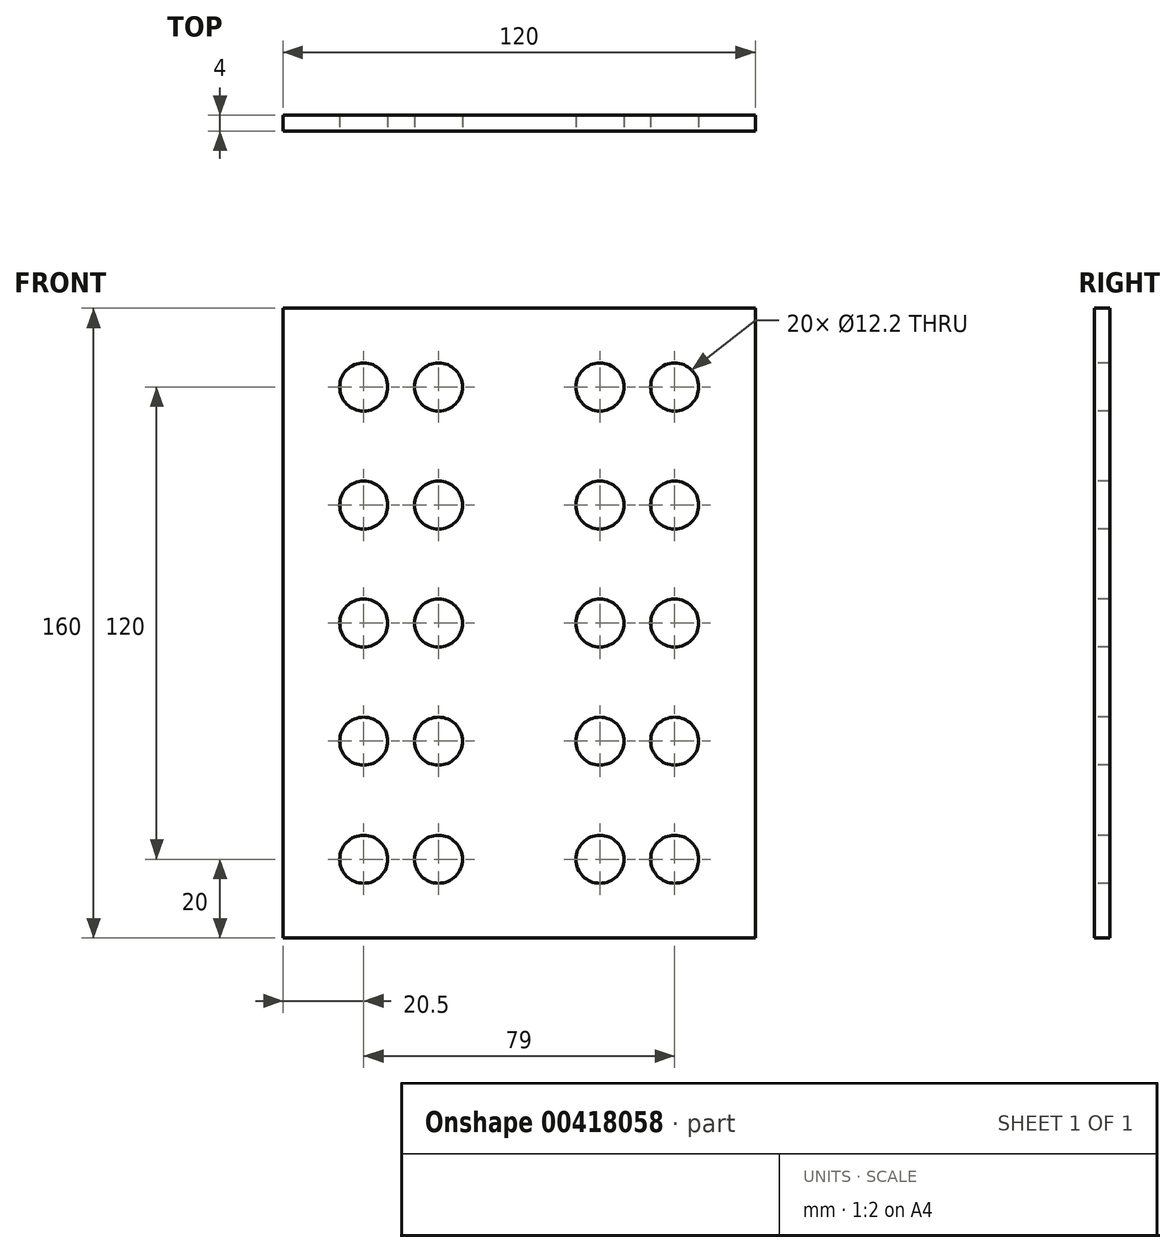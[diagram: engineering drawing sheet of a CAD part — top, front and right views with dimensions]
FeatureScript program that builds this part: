
annotation { "Feature Type Name" : "Feature", "Feature Type Description" : "" }
export const myFeature = defineFeature(function(context is Context, id is Id, definition is map)
    precondition{}
    {
        {
            var Q0;
            Q0=qCreatedBy(makeId("Front.planeOp"),FACE);
            var sketch = newSketch(context, id + "F0", { "sketchPlane" : qUnion([Q0])});
            skLineSegment(sketch, "E0.bottom", {"start": v(60, -80) * mm, "end": v(-60, -80) * mm});
            skLineSegment(sketch, "E0.top", {"start": v(60, 80) * mm, "end": v(-60, 80) * mm});
            skLineSegment(sketch, "E0.left", {"start": v(60, -80) * mm, "end": v(60, 80) * mm});
            skLineSegment(sketch, "E0.right", {"start": v(-60, -80) * mm, "end": v(-60, 80) * mm});
            skPoint(sketch, "E0.middle", {"position": v(0, 0) * mm});
            skCircle(sketch, "E1", {"center": v(-39.5, 0) * mm, "radius": 6.1 * mm});
            skCircle(sketch, "E2", {"center": v(-20.5, 0) * mm, "radius": 6.1 * mm});
            skLineSegment(sketch, "E3", {"start": v(-61.76, 0) * mm, "end": v(73.99, 0) * mm, "construction": true});
            skPoint(sketch, "E4", {"position": v(-30, 0) * mm});
            skLineSegment(sketch, "E5", {"start": v(-30, 4.5) * mm, "end": v(-30, -5.4) * mm, "construction": true});
            skLineSegment(sketch, "E6", {"start": v(0, 10.46) * mm, "end": v(0, -12.96) * mm, "construction": true});
            skCircle(sketch, "E7.MirrorC", {"center": v(20.5, 0) * mm, "radius": 6.1 * mm});
            skCircle(sketch, "E8.MirrorC", {"center": v(39.5, 0) * mm, "radius": 6.1 * mm});
            skCircle(sketch, "E9.0.1.0", {"center": v(-39.5, 30) * mm, "radius": 6.1 * mm});
            skCircle(sketch, "E9.0.1.1", {"center": v(-20.5, 30) * mm, "radius": 6.1 * mm});
            skCircle(sketch, "E9.0.1.2", {"center": v(20.5, 30) * mm, "radius": 6.1 * mm});
            skCircle(sketch, "E9.0.1.3", {"center": v(39.5, 30) * mm, "radius": 6.1 * mm});
            skCircle(sketch, "E9.0.2.0", {"center": v(-39.5, 60) * mm, "radius": 6.1 * mm});
            skCircle(sketch, "E9.0.2.1", {"center": v(-20.5, 60) * mm, "radius": 6.1 * mm});
            skCircle(sketch, "E9.0.2.2", {"center": v(20.5, 60) * mm, "radius": 6.1 * mm});
            skCircle(sketch, "E9.0.2.3", {"center": v(39.5, 60) * mm, "radius": 6.1 * mm});
            skLineSegment(sketch, "E9.direction1", {"start": v(-39.5, 0) * mm, "end": v(-15.1, 0) * mm, "construction": true});
            skLineSegment(sketch, "E9.direction2", {"start": v(-39.5, 0) * mm, "end": v(-39.5, 30) * mm, "construction": true});
            skCircle(sketch, "E10.0.1.0", {"center": v(-39.5, -30) * mm, "radius": 6.1 * mm});
            skCircle(sketch, "E10.0.1.1", {"center": v(-20.5, -30) * mm, "radius": 6.1 * mm});
            skCircle(sketch, "E10.0.1.2", {"center": v(20.5, -30) * mm, "radius": 6.1 * mm});
            skCircle(sketch, "E10.0.1.3", {"center": v(39.5, -30) * mm, "radius": 6.1 * mm});
            skCircle(sketch, "E10.0.2.0", {"center": v(-39.5, -60) * mm, "radius": 6.1 * mm});
            skCircle(sketch, "E10.0.2.1", {"center": v(-20.5, -60) * mm, "radius": 6.1 * mm});
            skCircle(sketch, "E10.0.2.2", {"center": v(20.5, -60) * mm, "radius": 6.1 * mm});
            skCircle(sketch, "E10.0.2.3", {"center": v(39.5, -60) * mm, "radius": 6.1 * mm});
            skLineSegment(sketch, "E10.direction1", {"start": v(-39.5, 0) * mm, "end": v(-14.5, 0) * mm, "construction": true});
            skLineSegment(sketch, "E10.direction2", {"start": v(-39.5, 0) * mm, "end": v(-39.5, -30) * mm, "construction": true});
            skSolve(sketch);
        }
        {
            var Q0;
            Q0=makeQuery(id+"F0.imprint","IMPRINT",FACE,{"disambiguationData":[TD([[makeQuery(id+"F0.imprint","IMPRINT",EDGE,{"derivedFrom":sQuery(id+"F0.wireOp",EDGE,"E0.bottom")}),-1.0]])]});
            extrude(context, id + "F1", {"entities" : qUnion([Q0]), "oppositeDirection" : true, "depth" : 4 * mm});
        }
    });
